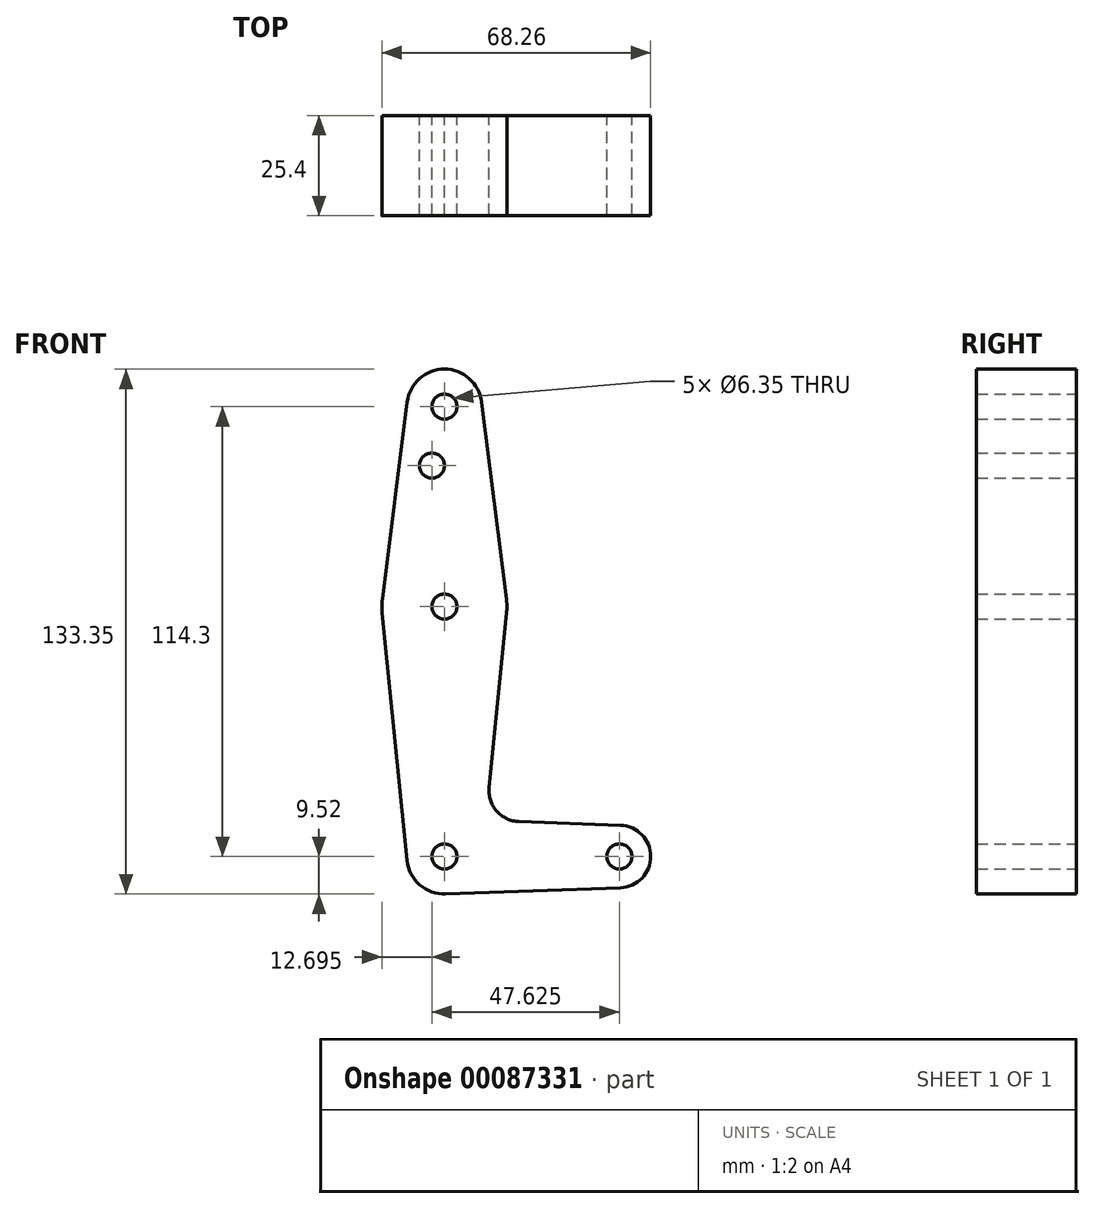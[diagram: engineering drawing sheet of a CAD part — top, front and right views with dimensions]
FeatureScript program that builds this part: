
annotation { "Feature Type Name" : "Feature", "Feature Type Description" : "" }
export const myFeature = defineFeature(function(context is Context, id is Id, definition is map)
    precondition{}
    {
        {
            var Q0;
            Q0=qCreatedBy(makeId("Front.planeOp"),FACE);
            var sketch = newSketch(context, id + "F0", { "sketchPlane" : qUnion([Q0])});
            skLineSegment(sketch, "E0", {"start": v(0, 0) * mm, "end": v(0, 114.3) * mm, "construction": true});
            skLineSegment(sketch, "E1", {"start": v(0, 0) * mm, "end": v(44.45, 0) * mm});
            skCircle(sketch, "E2", {"center": v(0, 114.3) * mm, "radius": 9.53 * mm});
            skCircle(sketch, "E3", {"center": v(0, 0) * mm, "radius": 9.53 * mm});
            skCircle(sketch, "E4", {"center": v(0, 63.5) * mm, "radius": 15.88 * mm});
            skLineSegment(sketch, "E5", {"start": v(-15.8, 61.91) * mm, "end": v(-9.48, -0.95) * mm});
            skLineSegment(sketch, "E6", {"start": v(-15.75, 65.48) * mm, "end": v(-9.45, 115.5) * mm});
            skLineSegment(sketch, "E7", {"start": v(9.45, 115.5) * mm, "end": v(15.75, 65.48) * mm});
            skLineSegment(sketch, "E8", {"start": v(15.8, 61.91) * mm, "end": v(11.34, 17.6) * mm});
            skCircle(sketch, "E9", {"center": v(44.45, 0) * mm, "radius": 7.94 * mm});
            skLineSegment(sketch, "E10", {"start": v(18.97, 8.85) * mm, "end": v(44.73, 7.93) * mm});
            skLineSegment(sketch, "E11", {"start": v(0.34, -9.52) * mm, "end": v(44.73, -7.93) * mm});
            skCircle(sketch, "E12", {"center": v(0, 114.3) * mm, "radius": 3.18 * mm});
            skCircle(sketch, "E13", {"center": v(-3.18, 99.33) * mm, "radius": 3.18 * mm});
            skCircle(sketch, "E14", {"center": v(0, 63.5) * mm, "radius": 3.18 * mm});
            skCircle(sketch, "E15", {"center": v(0, 0) * mm, "radius": 3.18 * mm});
            skCircle(sketch, "E16", {"center": v(44.45, 0) * mm, "radius": 3.18 * mm});
            skArc(sketch, "E17.filletArc", {"start": v(11.34, 17.6) * mm, "mid": v(13.26, 11.57) * mm, "end": v(18.97, 8.85) * mm});
            skSolve(sketch);
        }
        {
            var Q0;
            Q0=makeQuery(id+"F0.imprint","IMPRINT",FACE,{"disambiguationData":[TD([[makeQuery(id+"F0.imprint","IMPRINT",EDGE,{"derivedFrom":sQuery(id+"F0.wireOp",EDGE,"E12")}),-1.0]])]});
            var Q1;
            {var subQ1=sQuery(id+"F0.wireOp",EDGE,"E6");Q1=makeQuery(id+"F0.imprint","IMPRINT",FACE,{"disambiguationData":[TD([[makeQuery(id+"F0.imprint","IMPRINT",EDGE,{"derivedFrom":subQ1}),-1.0]])]});}
            var Q2;
            Q2=makeQuery(id+"F0.imprint","IMPRINT",FACE,{"disambiguationData":[TD([[makeQuery(id+"F0.imprint","IMPRINT",EDGE,{"derivedFrom":sQuery(id+"F0.wireOp",EDGE,"E14")}),-1.0]])]});
            var Q3;
            {var subQ5=sQuery(id+"F0.wireOp",EDGE,"E5");Q3=makeQuery(id+"F0.imprint","IMPRINT",FACE,{"disambiguationData":[TD([[makeQuery(id+"F0.imprint","IMPRINT",EDGE,{"derivedFrom":subQ5}),1.0]])]});}
            var Q4;
            Q4=makeQuery(id+"F0.imprint","IMPRINT",FACE,{"disambiguationData":[TD([[makeQuery(id+"F0.imprint","IMPRINT",EDGE,{"derivedFrom":sQuery(id+"F0.wireOp",EDGE,"E15")}),-1.0]])]});
            var Q5;
            {var subQ0=sQuery(id+"F0.wireOp",EDGE,"E8");var subQ1=sQuery(id+"F0.wireOp",EDGE,"E1");var subQ2=makeQuery(id+"F0.imprint","INTERSECT",VERTEX,{"derivedFrom":[subQ1,subQ0]});Q5=makeQuery(id+"F0.imprint","IMPRINT",FACE,{"disambiguationData":[TD([[makeQuery(id+"F0.imprint","IMPRINT",EDGE,{"disambiguationData":[TD([[subQ2,-1.0]])],"derivedFrom":subQ1}),1.0]])]});}
            var Q6;
            {var subQ0=sQuery(id+"F0.wireOp",EDGE,"E11");Q6=makeQuery(id+"F0.imprint","IMPRINT",FACE,{"disambiguationData":[TD([[makeQuery(id+"F0.imprint","IMPRINT",EDGE,{"derivedFrom":subQ0}),1.0]])]});}
            var Q7;
            {var subQ0=sQuery(id+"F0.wireOp",EDGE,"E8");var subQ1=sQuery(id+"F0.wireOp",EDGE,"E1");var subQ2=makeQuery(id+"F0.imprint","INTERSECT",VERTEX,{"derivedFrom":[subQ1,subQ0]});Q7=makeQuery(id+"F0.imprint","IMPRINT",FACE,{"disambiguationData":[TD([[makeQuery(id+"F0.imprint","IMPRINT",EDGE,{"disambiguationData":[TD([[subQ2,1.0]])],"derivedFrom":subQ1}),1.0]])]});}
            var Q8;
            Q8=makeQuery(id+"F0.imprint","IMPRINT",FACE,{"disambiguationData":[TD([[makeQuery(id+"F0.imprint","IMPRINT",EDGE,{"derivedFrom":sQuery(id+"F0.wireOp",EDGE,"E16")}),-1.0]])]});
            extrude(context, id + "F1", {"entities" : qUnion([Q0, Q1, Q2, Q3, Q4, Q5, Q6, Q7, Q8]), "depth" : 25.4 * mm});
        }
    });
